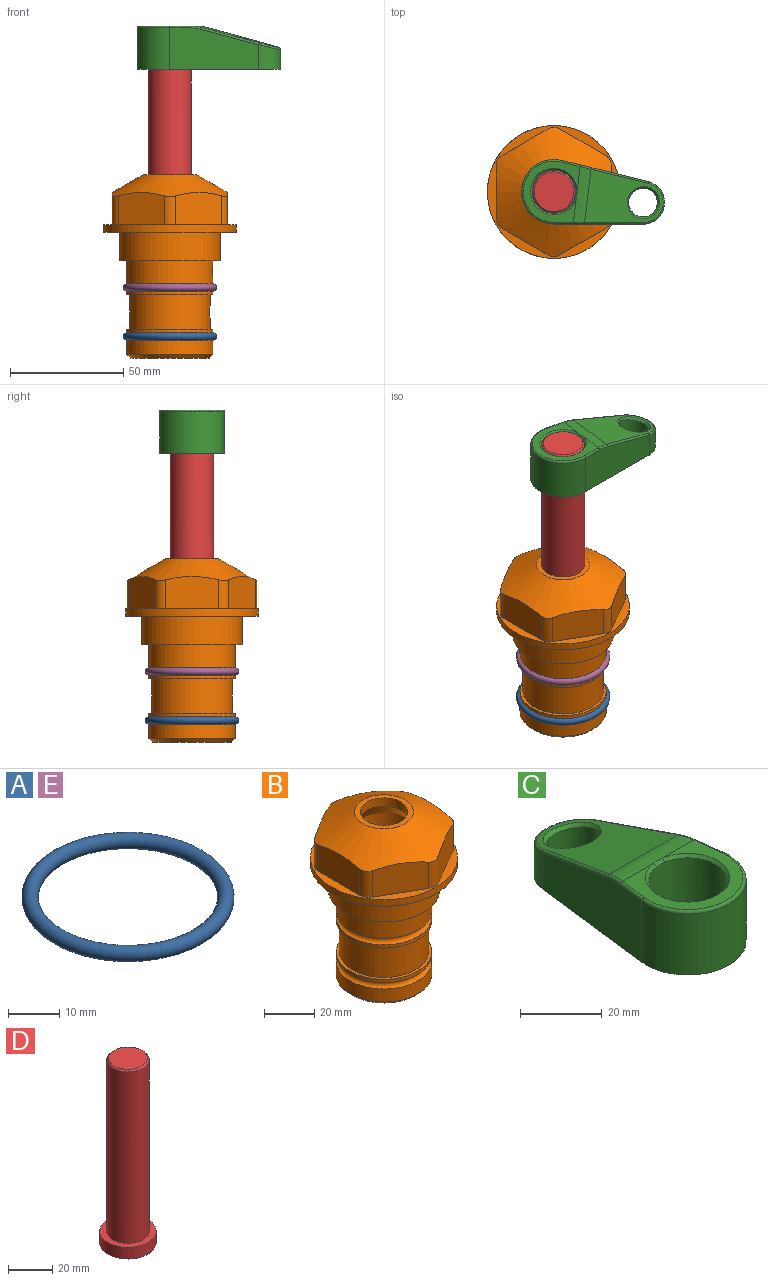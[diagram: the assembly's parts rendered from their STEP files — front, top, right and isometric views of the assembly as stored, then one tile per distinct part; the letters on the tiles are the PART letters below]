
ASSEMBLY  parts=5 mates=4
PART A: 1 faces, bbox 44.7x44.7x3.2 mm
  f0: torus R=19.05mm, axis (0,0,1), area 1193.9mm2
PART B: 36 faces, bbox 58.7x58.7x81 mm
  f0: cylinder r=17.78mm len=35.56mm, axis (0,0,1), area 1670.8mm2, adj f23,f24,f31
  f1: cylinder r=19.05mm len=38.1mm, axis (0,0,1), area 1191.9mm2, adj f26,f27,f30
  f2: plane 58.66x58.66mm, normal (0,0,-1), area 1150.6mm2, adj f3,f28
  f3: cylinder r=29.33mm len=58.66mm, axis (0,0,-1), area 585.1mm2, adj f2,f4
  f4: plane 58.66x58.66mm, normal (0,0,1), area 475.9mm2, adj f3,f5,f6,f7,f8,f9,f10,f11
  f5: plane 20.32x14.34mm, normal (-0.5,0.87,0), area 324.4mm2, adj f4,f15,f16,f17
  f6: plane 20.32x14.34mm, normal (0.5,0.87,0), area 324.4mm2, adj f4,f14,f15,f17
  f7: plane 23.48x14.34mm, normal (1,0,0), area 324.4mm2, adj f4,f13,f14,f17
  f8: plane 20.32x14.34mm, normal (0.5,-0.87,0), area 324.4mm2, adj f4,f12,f13,f17
  f9: plane 20.32x14.34mm, normal (-0.5,-0.87,0), area 324.4mm2, adj f4,f11,f12,f17
  f10: plane 23.48x14.34mm, normal (-1,0,0), area 324.4mm2, adj f4,f11,f16,f17
  f11: cylinder r=5.08mm len=12.85mm, axis (0,0,-1), area 67.2mm2, adj f4,f9,f10,f17
  f12: cylinder r=5.08mm len=12.85mm, axis (0,0,-1), area 67.2mm2, adj f4,f8,f9,f17
  f13: cylinder r=5.08mm len=12.85mm, axis (0,0,-1), area 67.2mm2, adj f4,f7,f8,f17
  f14: cylinder r=5.08mm len=12.85mm, axis (0,0,-1), area 67.2mm2, adj f4,f6,f7,f17
  f15: cylinder r=5.08mm len=12.85mm, axis (0,0,-1), area 67.2mm2, adj f4,f5,f6,f17
  f16: cylinder r=5.08mm len=12.85mm, axis (0,0,-1), area 67.2mm2, adj f4,f5,f10,f17
  f17: cone r=11.73mm half-angle=60deg, axis (0,0,-1), area 2071.8mm2, adj f5,f6,f7,f8,f9,f10,f11,f12
  f18: plane 23.46x23.46mm, normal (0,0,1), area 147.4mm2, adj f17,f35
  f19: plane 34.93x34.93mm, normal (0,0,-1), area 958mm2, adj f29
  f20: cylinder r=19.05mm len=38.1mm, axis (0,0,1), area 760.1mm2, adj f21,f29
  f21: torus R=19.05mm, axis (0,0,1), area 565.3mm2, adj f20,f22
  f22: cylinder r=19.05mm len=38.1mm, axis (0,0,1), area 190mm2, adj f21,f23
  f23: plane 38.1x38.1mm, normal (0,0,1), area 146.9mm2, adj f0,f22
  f24: plane 38.1x38.1mm, normal (0,0,-1), area 146.9mm2, adj f0,f25
  f25: cylinder r=19.05mm len=38.1mm, axis (0,0,1), area 190mm2, adj f24,f26
  f26: torus R=19.05mm, axis (0,0,1), area 565.3mm2, adj f1,f25
  f27: plane 44.45x44.45mm, normal (0,0,-1), area 411.7mm2, adj f1,f28
  f28: cylinder r=22.23mm len=44.45mm, axis (0,0,1), area 1773.5mm2, adj f2,f27
  f29: cone r=19.05mm half-angle=45deg, axis (0,0,1), area 257.5mm2, adj f19,f20
  f30: cylinder r=3.17mm len=6.75mm, axis (-1,0,0), area 128mm2, adj f1,f33
  f31: cylinder r=3.17mm len=6.35mm, axis (-1,0,0), area 102.5mm2, adj f0,f33
  f32: plane 25.4x25.4mm, normal (0,0,1), area 506.7mm2, adj f33
  f33: cylinder r=12.7mm len=66.42mm, axis (0,0,-1), area 5236.2mm2, adj f30,f31,f32,f34
  f34: cone r=9.53mm half-angle=30deg, axis (0,0,-1), area 443.4mm2, adj f33,f35
  f35: cylinder r=9.53mm len=19.05mm, axis (0,0,-1), area 240.9mm2, adj f18,f34
PART C: 31 faces, bbox 31.7x65.5x19.8 mm
  f0: plane 39.12x18.26mm, normal (0.99,0.12,0), area 612.2mm2, adj f1,f4,f7,f11,f13,f15
  f1: cylinder r=9.53mm len=18.91mm, axis (0,0,-1), area 296.1mm2, adj f0,f2,f7,f17
  f2: plane 39.12x18.26mm, normal (-0.99,0.12,0), area 612.2mm2, adj f1,f4,f7,f12,f14,f16
  f3: cylinder r=6.35mm len=12.7mm, axis (0,0,-1), area 362.4mm2, adj f7,f18
  f4: cylinder r=14.29mm len=28.58mm, axis (0,0,-1), area 882.2mm2, adj f0,f2,f7,f10
  f5: cylinder r=9.53mm len=19.05mm, axis (0,0,-1), area 1092.6mm2, adj f7,f19,f20
  f6: plane 26.99x23.69mm, normal (0,0,1), area 216.2mm2, adj f9,f10,f11,f12,f19
  f7: plane 63.5x28.58mm, normal (0,0,-1), area 661.8mm2, adj f0,f1,f2,f3,f4,f5,f22,f23
  f8: plane 33.52x23.6mm, normal (0,0.26,0.97), area 486mm2, adj f9,f15,f16,f17,f18
  f9: cylinder r=19.05mm len=24.72mm, axis (1,0,0), area 120.4mm2, adj f6,f8,f13,f14,f20
  f10: torus R=13.49mm, axis (0,0,1), area 59mm2, adj f4,f6,f11,f12
  f11: cylinder r=0.79mm len=8.67mm, axis (0.12,-0.99,0), area 10.8mm2, adj f0,f6,f10,f13
  f12: cylinder r=0.79mm len=8.67mm, axis (0.12,0.99,0), area 10.8mm2, adj f2,f6,f10,f14
  f13: bspline ~4.95x1.42mm, area 6.1mm2, adj f0,f9,f11,f15
  f14: bspline ~4.95x1.42mm, area 6.1mm2, adj f2,f9,f12,f16
  f15: cylinder r=0.79mm len=25.95mm, axis (0.12,-0.96,0.26), area 32.9mm2, adj f0,f8,f13,f17
  f16: cylinder r=0.79mm len=25.95mm, axis (0.12,0.96,-0.26), area 32.9mm2, adj f2,f8,f14,f17
  f17: bspline ~18.91x8.38mm, area 30mm2, adj f1,f8,f15,f16
  f18: bspline ~14.29x14.29mm, area 48.3mm2, adj f3,f8
  f19: cone r=9.53mm half-angle=45deg, axis (0,0,1), area 66.5mm2, adj f5,f6,f20
  f20: bspline ~3.22x0.96mm, area 3.5mm2, adj f5,f9,f19
  f21: plane 2.75x2.72mm, normal (0,0,-1), area 2.9mm2, adj f23,f25,f28
  f22: plane 23.05x15.88mm, normal (-0.99,-0.12,0), area 323.6mm2, adj f7,f25,f26,f27,f28,f29
  f23: plane 23.05x15.88mm, normal (0.99,-0.12,0), area 323.6mm2, adj f7,f21,f25,f27,f28,f30
  f24: cylinder r=9.53mm len=10.69mm, axis (0,0,-1), area 114.7mm2, adj f7,f27,f29,f30
  f25: cylinder r=12.7mm len=20.59mm, axis (0,0,-1), area 381.1mm2, adj f7,f21,f22,f23,f26,f28
  f26: plane 2.75x2.72mm, normal (0,0,-1), area 2.9mm2, adj f22,f25,f28
  f27: plane 19.72x18.37mm, normal (0,-0.26,-0.97), area 291.8mm2, adj f22,f23,f24,f28,f29,f30
  f28: cylinder r=15.88mm len=19.92mm, axis (1,0,0), area 54.8mm2, adj f21,f22,f23,f25,f26,f27
  f29: cylinder r=1.59mm len=11mm, axis (0,0,-1), area 34.7mm2, adj f7,f22,f24,f27
  f30: cylinder r=1.59mm len=11mm, axis (0,0,-1), area 34.7mm2, adj f7,f23,f24,f27
PART D: 6 faces, bbox 25.4x25.4x101.6 mm
  f0: plane 17.46x17.46mm, normal (0,0,1), area 239.5mm2, adj f5
  f1: plane 25.4x25.4mm, normal (0,0,-1), area 506.7mm2, adj f2
  f2: cylinder r=12.7mm len=25.4mm, axis (0,0,1), area 506.7mm2, adj f1,f3
  f3: plane 25.4x25.4mm, normal (0,0,1), area 221.7mm2, adj f2,f4
  f4: cylinder r=9.53mm len=94.46mm, axis (0,0,1), area 5653mm2, adj f3,f5
  f5: cone r=8.73mm half-angle=45deg, axis (0,0,-1), area 64.4mm2, adj f0,f4
PART E: same geometry as A
PLACE A t=(0,0,-21.59)mm
PLACE B at identity fixed
PLACE C rot(axis=(0,0,-1),97deg) t=(0,0,27.55)mm
PLACE D rot(axis=(0,0,-1),97deg) t=(0,0,27.55)mm
PLACE E at identity
MATE cylindrical D.f2 <-> B.f0  axis (0,0,-1) through (0,0,-10.55)mm
MATE fastened D.f2 <-> C.f4  axis (0,0,1) through (0,0,91.05)mm
MATE fastened B.f0 <-> A.f0  axis (0,0,1) through (0,0,-46.1)mm
MATE fastened B.f0 <-> E.f0  axis (0,0,1) through (0,0,-24.51)mm
